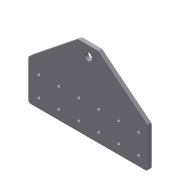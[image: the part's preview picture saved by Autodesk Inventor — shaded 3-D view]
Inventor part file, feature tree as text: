
AUTODESK INVENTOR PART (.ipt)
format: ipt  version: 2012 (Build 160160000, 160)  size: 124,928 bytes
history: native  units: in
note: dims shown in document units (in); Inventor stores cm internally (conversion verified against a paired STEP export)
features: extrude x4, sketch x4, pattern_linear x1, fillet x1
ambient origin geometry x8: Origin, YZ Plane, XZ Plane, XY Plane, X Axis, Y Axis, Z Axis, Center Point
bodies: Solid1 (feature_tree)
feature tree (10):
  extrude  "Extrusion1"  Depth=4.0in
  extrude  "Extrusion2"  Depth=3.0in
  extrude  "Extrusion3"  Depth=0.1875in TaperAngle=0.0deg
  pattern_linear  "Rectangular Pattern1"  Spacing1=0.5in  [1 undecoded]
  extrude  "Extrusion4"  Depth=0.5in
  fillet  "Fillet1"  Radius=0.1875in
  sketch  "Sketch1"  dims[d0=6.0in d1=4.0in]
  sketch  "Sketch2"  dims[d2=0.1875in d3=0.0in d4=3.0in]
  sketch  "Sketch3"  dims[d5=0.5in d6=0.1875in d7=0.0in]
  sketch  "Sketch4"  dims[d8=0.1875in d9=0.5in d10=0.5in d11=0.1875in d12=0.0in d13=2.3622in d15=1.0in d16=0.7874in d18=1.0in d19=2.5in d20=2.5in d21=2.0in d22=0.1875in d23=0.0in d24=0.125in d25=0.375in]
note: 1 required parameter value undecoded (feature->parameter linkage not recoverable at this tier; creation-order binding heuristic only, values carry confidence <= 0.55)
